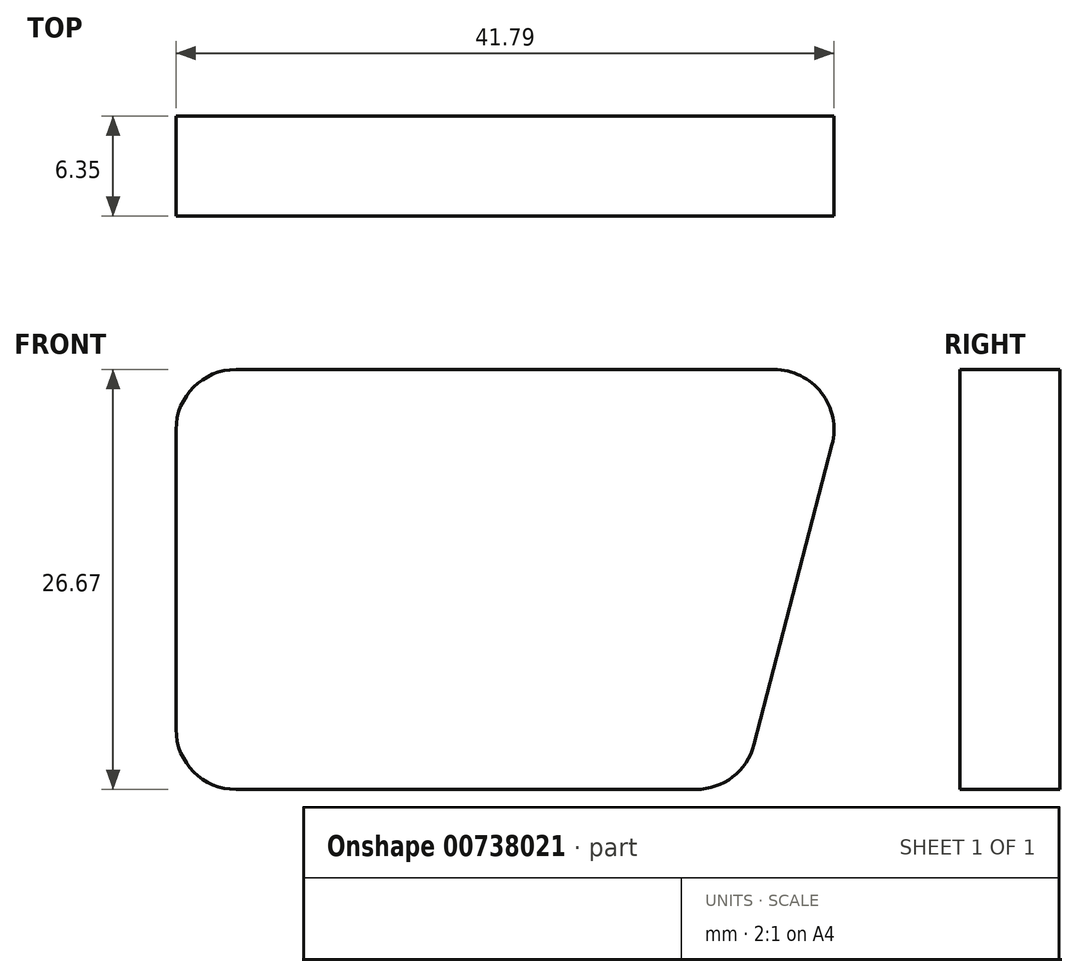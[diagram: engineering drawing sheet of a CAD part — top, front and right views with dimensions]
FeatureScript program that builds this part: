
annotation { "Feature Type Name" : "Feature", "Feature Type Description" : "" }
export const myFeature = defineFeature(function(context is Context, id is Id, definition is map)
    precondition{}
    {
        {
            var Q0;
            Q0=qCreatedBy(makeId("Front.planeOp"),FACE);
            var sketch = newSketch(context, id + "F0", { "sketchPlane" : qUnion([Q0])});
            skLineSegment(sketch, "E0", {"start": v(-32.1, 22.74) * mm, "end": v(-32.1, 3.7) * mm});
            skLineSegment(sketch, "E1", {"start": v(-28.3, -0.12) * mm, "end": v(0.92, -0.12) * mm});
            skLineSegment(sketch, "E2", {"start": v(4.6, 2.73) * mm, "end": v(9.56, 21.78) * mm});
            skLineSegment(sketch, "E3", {"start": v(5.88, 26.55) * mm, "end": v(-28.3, 26.55) * mm});
            skPoint(sketch, "E4.visualSharp", {"position": v(3.86, -0.12) * mm});
            skArc(sketch, "E4.filletArc", {"start": v(0.92, -0.12) * mm, "mid": v(3.25, 0.68) * mm, "end": v(4.6, 2.73) * mm});
            skPoint(sketch, "E5.visualSharp", {"position": v(10.8, 26.55) * mm});
            skArc(sketch, "E5.filletArc", {"start": v(9.56, 21.78) * mm, "mid": v(8.9, 25.07) * mm, "end": v(5.88, 26.55) * mm});
            skPoint(sketch, "E6.visualSharp", {"position": v(-32.1, 26.55) * mm});
            skArc(sketch, "E6.filletArc", {"start": v(-28.3, 26.55) * mm, "mid": v(-30.99, 25.43) * mm, "end": v(-32.1, 22.74) * mm});
            skPoint(sketch, "E7.visualSharp", {"position": v(-32.1, -0.12) * mm});
            skArc(sketch, "E7.filletArc", {"start": v(-32.1, 3.7) * mm, "mid": v(-30.99, 1) * mm, "end": v(-28.3, -0.12) * mm});
            skSolve(sketch);
        }
        {
            var Q0;
            Q0 = qSketchRegion(id + "F0", true);
            extrude(context, id + "F1", {"entities" : qUnion([Q0]), "depth" : 6.35 * mm, "offsetDistance" : 25.4 * mm});
        }
    });
